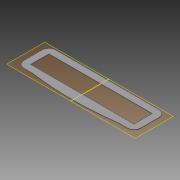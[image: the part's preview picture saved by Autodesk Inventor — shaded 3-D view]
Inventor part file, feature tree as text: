
AUTODESK INVENTOR PART (.ipt)
format: ipt  version: 2014 SP1 (Build 180222100, 222)  size: 111,616 bytes
history: native  units: mm
features: extrude x3, sketch x3
ambient origin geometry x8: Origin, YZ Plane, XZ Plane, XY Plane, X Axis, Y Axis, Z Axis, Center Point
bodies: Solid1 (feature_tree)
feature tree (6):
  extrude  "Extrusion1"  Depth=38.0mm
  extrude  "Extrusion2"  Depth=140.0mm
  extrude  "Extrusion3"  Depth=8.0mm
  sketch  "Sketch1"  dims[d0=19.0mm d1=38.0mm]
  sketch  "Sketch2"  dims[d2=140.0mm d3=70.0mm]
  sketch  "Sketch3"  dims[d4=8.0mm d5=8.0mm d6=0.5mm d7=0.0mm d12=3.5mm d17=0.5mm d18=0.0mm d19=0.0mm d20=0.0mm d24=30.0mm d25=30.0mm d26=18.0mm d27=15.0mm d28=15.0mm d30=2.0mm d31=18.0mm d32=5.5mm]
